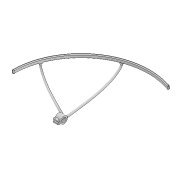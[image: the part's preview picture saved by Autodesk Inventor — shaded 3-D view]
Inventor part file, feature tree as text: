
AUTODESK INVENTOR PART (.ipt)
format: ipt  version: 2022 (Build 260153000, 153)  size: 822,784 bytes
history: native  units: mm
features: sketch x13, plane x7, extrude x6, projected_geometry x5, loft x4, fillet x2
ambient origin geometry x8: Origin, YZ Plane, XZ Plane, XY Plane, X Axis, Y Axis, Z Axis, Center Point
bodies: Solid1 (feature_tree)
feature tree (37):
  extrude  "Extrusion1"  Depth=5.0mm
  plane  "Work Plane1"
  sketch  "Sketch11"  dims[d2=10.0mm d3=0.0mm d4=38.724mm]
  sketch  "Sketch12"  dims[d23=5.0mm d24=30.0mm]
  plane  "Work Plane6"
  sketch  "Sketch13"  dims[d25=6.0mm d33=12.217305mm]
  sketch  "Sketch14"  dims[d35=3.490659mm d42=5.0mm]
  plane  "Work Plane7"
  plane  "Work Plane8"
  loft  "Loft4"
  plane  "Work Plane9"
  loft  "Loft5"
  plane  "Work Plane10"
  sketch  "Sketch20"  dims[d61=0.0mm d62=90.0deg d63=5.0mm]
  extrude  "Extrusion2"  Depth=12.217305mm
  extrude  "Extrusion3"  Depth=5.0mm
  sketch  "Sketch21"  dims[d64=50.0mm d65=-47.0mm d66=12.1mm d67=19.0mm]
  extrude  "Extrusion4"  TaperAngle=0.0deg  [1 undecoded]
  extrude  "Extrusion5"  Depth=6.0mm
  extrude  "Extrusion6"  TaperAngle=0.0deg  [1 undecoded]
  plane  "Work Plane11"
  sketch  "Sketch28"  dims[d72=1.5mm d73=6.0mm d74=15.0mm d75=0.0mm d76=3.0mm d77=3.0mm d78=15.0mm d79=0.0mm d80=2.2mm d81=2.2mm d82=3.0mm d83=4.0mm d84=4.0mm d85=3.0mm d86=15.0mm d87=0.0mm d89=3.0mm d98=9.0mm d99=9.0mm d110=3.490659mm d111=3.490659mm d113=9.0mm d114=9.0mm d115=0.0mm d116=90.0deg d117=0.0mm d118=90.0deg d119=0.0mm d120=90.0deg d121=0.0mm d122=90.0deg d123=2.0mm d124=2.0mm]
  sketch  "Sketch27"  dims[d70=15.0mm d71=0.0mm]
  loft  "Loft10"
  loft  "Loft11"
  fillet  "Fillet4"  Radius=12.1mm
  fillet  "Fillet5"  Radius=19.0mm
  sketch  "Sketch1"  dims[d0=371.0mm d1=5.0mm]
  sketch  "Sketch17"  dims[d50=0.0mm d51=90.0deg d52=0.0mm d53=90.0deg]
  sketch  "Sketch18"  dims[d54=0.0mm d55=90.0deg d56=6.0mm]
  sketch  "Sketch19"  dims[d57=0.0mm d58=90.0deg d59=0.0mm d60=90.0deg]
  projected_geometry  "Projected Loop3"
  sketch  "Sketch22"  dims[d68=15.0mm d69=0.0mm]
  projected_geometry  "Projected Loop10"
  projected_geometry  "Projected Loop11"
  projected_geometry  "Projected Loop12"
  projected_geometry  "Project Cut Edges3"
note: 2 required parameter values undecoded (feature->parameter linkage not recoverable at this tier; creation-order binding heuristic only, values carry confidence <= 0.55)
